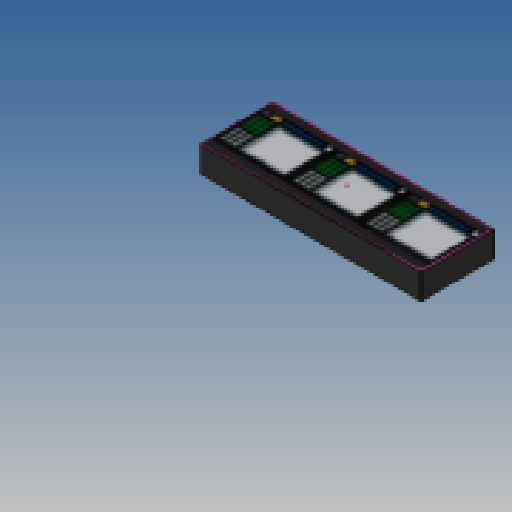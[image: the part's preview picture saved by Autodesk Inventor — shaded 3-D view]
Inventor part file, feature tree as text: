
AUTODESK INVENTOR PART (.ipt)
format: ipt  version: 2025 (Build 290162010, 162A)  size: 185,344 bytes
history: native  units: in
note: dims shown in document units (in); Inventor stores cm internally (conversion verified against a paired STEP export)
features: other x4, extrude x3, sketch x3, fillet x1
ambient origin geometry x8: Origin, YZ Plane, XZ Plane, XY Plane, X Axis, Y Axis, Z Axis, Center Point
bodies: Solid1 (feature_tree)
feature tree (11):
  extrude  "Extrusion1"  Depth=0.315in
  sketch  "Sketch3"  dims[d4=0.126in d5=0.0in d7=0.0591in d8=0.063in]
  extrude  "Extrusion2"  Depth=0.063in
  extrude  "Extrusion7"  Depth=0.0039in
  fillet  "Fillet1"  Radius=0.2564in
  other  "Work Axis1"
  other  "Work Axis2"
  other  "Aufkleber1"
  sketch  "Sketch2"  dims[d0=0.9449in d1=0.315in]
  sketch  "Skizze10"  dims[d11=0.063in d12=0.0in d22=0.0039in d60=0.2564in d61=0.189in d62=0.063in d75=0.315in d76=0.315in d86=0.126in d89=0.315in d90=0.0in d91=0.0in d92=0.0in d93=0.0in d94=0.0in d95=0.0157in d96=0.0157in d97=0.0157in d98=0.0in]
  other  "Bild2"
